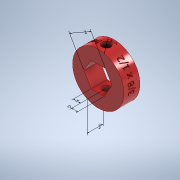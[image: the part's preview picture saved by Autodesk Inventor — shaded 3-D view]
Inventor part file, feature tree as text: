
AUTODESK INVENTOR PART (.ipt)
format: ipt  version: 2022.1 (Build 261234000, 234)  size: 1,182,720 bytes
history: native  units: in
note: dims shown in document units (in); Inventor stores cm internally (conversion verified against a paired STEP export)
features: other x6, sketch x4, extrude x2, thicken_offset x1, plane x1, emboss x1, hole x1
ambient origin geometry x8: Origin, YZ Plane, XZ Plane, XY Plane, X Axis, Y Axis, Z Axis, Center Point
bodies: Solid1 (feature_tree)
feature tree (16):
  other  "Annotations"
  extrude  "Extrusion1"  Depth=1.125in
  thicken_offset  "Thicken2"
  plane  "Work Plane1"
  emboss  "Emboss1"
  hole  "Hole1"  [1 undecoded]
  extrude  "Extrusion2"  Depth=0.0225in
  sketch  "Sketch1"  dims[d0=0.5in d2=1.125in]
  sketch  "Sketch2"  dims[d3=0.2738in d4=0.375in d5=0.0in]
  sketch  "Sketch3"  dims[d8=0.0225in d9=0.0225in]
  sketch  "Sketch4"  dims[d17=1.0in d18=0.25in d19=0.1in d20=0.0in d21=0.17in d22=0.75in d23=0.5in d24=0.093in d25=0.5635in d26=1.0in d27=0.8108in d28=0.1763in d29=0.1763in d30=0.191in d31=0.2186in d32=0.0in d10=0.5245in d11=1.125in d12=0.1538in d13=0.545in d14=0.1112in d15=0.3058in d16=0.3525in d33=0.2141in d34=0.1573in d35=0.2997in d36=0.1313in]
  other  "Diameter Dimension 1"
  other  "Linear Dimension 1"
  other  "Linear Dimension 2"
  other  "Linear Dimension 3"
  other  "Linear Dimension 4"
note: 1 required parameter value undecoded (feature->parameter linkage not recoverable at this tier; creation-order binding heuristic only, values carry confidence <= 0.55)
